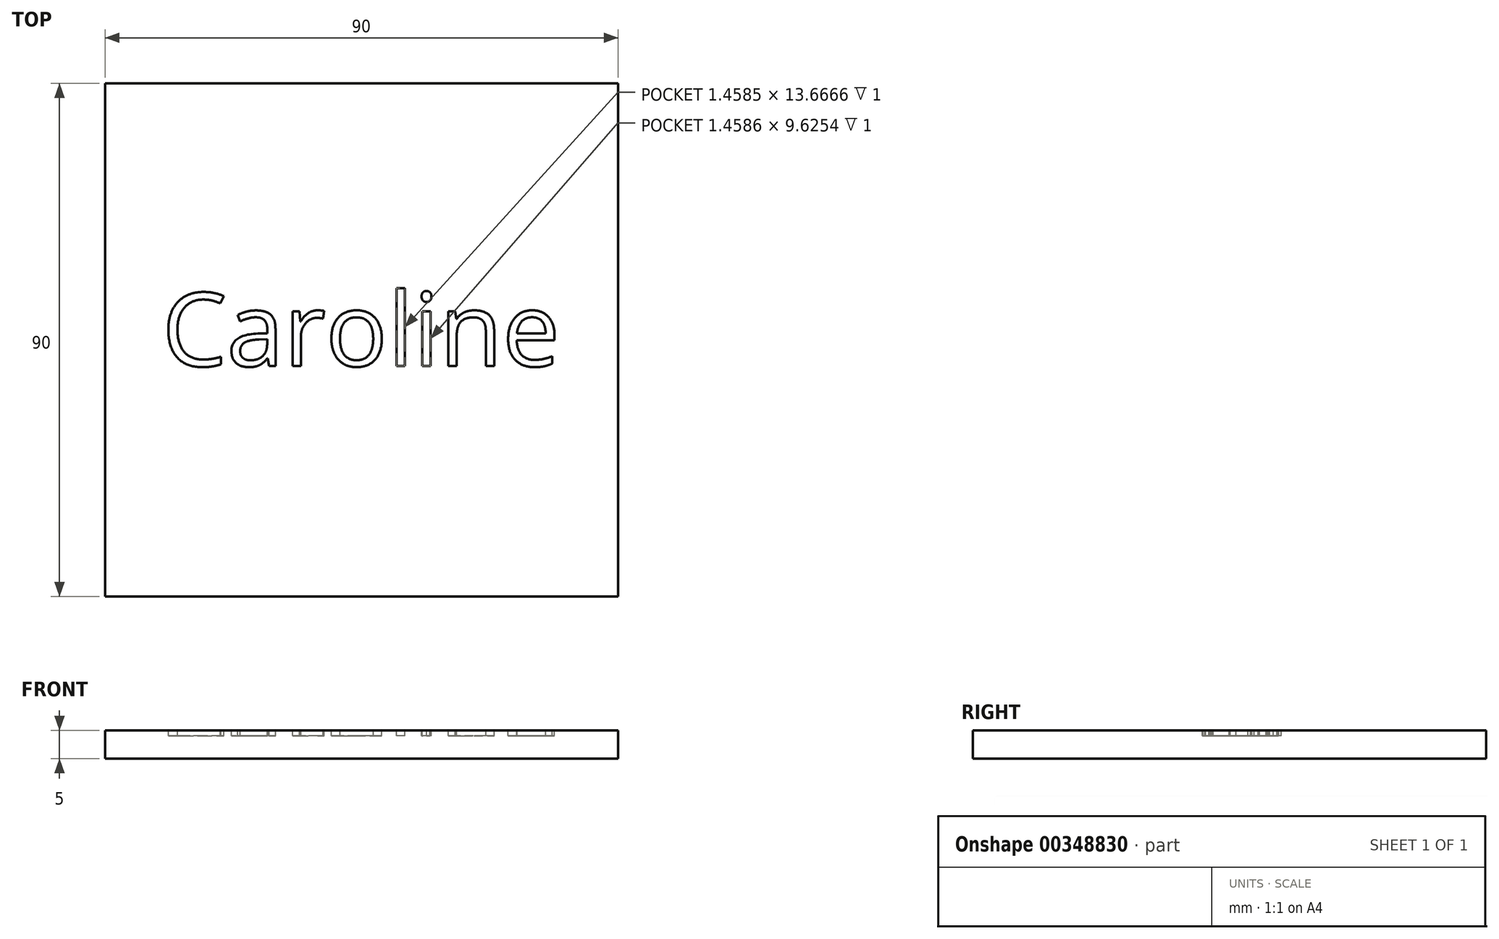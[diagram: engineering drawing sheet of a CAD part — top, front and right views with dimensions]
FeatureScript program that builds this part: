
annotation { "Feature Type Name" : "Feature", "Feature Type Description" : "" }
export const myFeature = defineFeature(function(context is Context, id is Id, definition is map)
    precondition{}
    {
        {
            var Q0;
            Q0=qCreatedBy(makeId("Top.planeOp"),FACE);
            var sketch = newSketch(context, id + "F0", { "sketchPlane" : qUnion([Q0])});
            skLineSegment(sketch, "E0.bottom", {"start": v(-45, -45) * mm, "end": v(45, -45) * mm});
            skLineSegment(sketch, "E0.top", {"start": v(-45, 45) * mm, "end": v(45, 45) * mm});
            skLineSegment(sketch, "E0.left", {"start": v(-45, -45) * mm, "end": v(-45, 45) * mm});
            skLineSegment(sketch, "E0.right", {"start": v(45, -45) * mm, "end": v(45, 45) * mm});
            skSolve(sketch);
        }
        {
            var Q0;
            Q0 = qSketchRegion(id + "F0", true);
            extrude(context, id + "F1", {"entities" : qUnion([Q0]), "depth" : 5 * mm});
        }
        {
            var Q0;
            Q0=makeQuery(id+"F1.opExtrude","CAP_FACE",FACE,{"disambiguationData":[OSD([sQuery(id+"F0.wireOp",EDGE,"E0.bottom"),sQuery(id+"F0.wireOp",EDGE,"E0.top"),sQuery(id+"F0.wireOp",EDGE,"E0.left"),sQuery(id+"F0.wireOp",EDGE,"E0.right")])],"isStart":false});
            var sketch = newSketch(context, id + "F2", { "sketchPlane" : qUnion([Q0])});
            skText(sketch, "E1", { "text": "Caroline", "fontName": "OpenSans-Regular.ttf"});
            const initialGuessF2  = {"E1": [-0.035, -0.00461, 1, 0, 0.01295]};
            skSetInitialGuess(sketch, initialGuessF2);
            skSolve(sketch);
        }
        {
            var Q0;
            Q0 = qSketchRegion(id + "F2", true);
            extrude(context, id + "F3", {"entities" : qUnion([Q0]), "operationType" : NewBodyOperationType.REMOVE, "oppositeDirection" : true, "depth" : 1 * mm});
        }
    });
